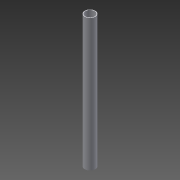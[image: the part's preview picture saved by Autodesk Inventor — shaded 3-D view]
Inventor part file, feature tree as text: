
AUTODESK INVENTOR PART (.ipt)
format: ipt  version: 2015 (Build 190159000, 159)  size: 114,176 bytes
history: native  units: mm
features: sketch x2, extrude x1, shell x1, hole x1
ambient origin geometry x8: Origin, YZ Plane, XZ Plane, XY Plane, X Axis, Y Axis, Z Axis, Center Point
bodies: Body1 (feature_tree)
feature tree (5):
  extrude  "Wyciągnięcie proste2"  Depth=32.0mm
  shell  "Skorupa2"  Thickness=400.0mm
  hole  "Otwór1"  [1 undecoded]
  sketch  "Szkic2"
  sketch  "Szkic3"
note: 1 required parameter value undecoded (feature->parameter linkage not recoverable at this tier; creation-order binding heuristic only, values carry confidence <= 0.55)
